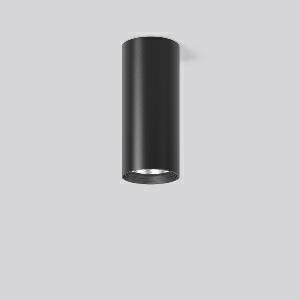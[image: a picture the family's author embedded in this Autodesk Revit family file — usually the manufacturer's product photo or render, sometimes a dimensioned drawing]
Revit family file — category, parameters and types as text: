
# Revit family: heledon_mini_a_931201_003_3_76_2d51
name_source: partatom
category: Lighting Fixtures
units: mm (PartAtom-declared; Revit-internal decimal feet)

## family parameters
Cut with Voids When Loaded = No
Host = Face
Light Source = No
Part Type = Normal
Room Calculation Point = No
Round Connector Dimension = Use Diameter
Shared = No

## types (1)
- HELEDON mini A (1 x LED Modul 935, 2500 lm, 3500)
    Apparent Load = 20 VA
    Approval mark = CE
    CIE Flux Codes = 99 100 100 100 100
    Color Rendering = 92
    Color Temperature = 3500
    Default Elevation = 1800 mm
    Description = Series: HELEDON mini
Cylindrical surface-mounted downlight. Housing: die-cast aluminium, powder-coated. Internal ceiling frame polycarbonate with bayonet mounting. Black plastic ring and recessed LED to prevent glare from the side. Optical assembly with reflector made of MIRO-Silver with 98% total light reflection for outstanding efficiency - can be changed without tools. Best colour rendering index Ra>90. Suitable for Ceiling mounting. Easy installation with a separate ceiling frame with bayonet mounting and plug connection. Driver integrated. Connected via plug-in connector. High quality converter without flickering and stroboscopic effect. The following accessories can be mounted without use of tools: interchangeable lenses, decorative glasses, honeycomb louvre, clear and frosted diffusers, white interchangeable plastic ring. 
Colour: deep black, matt (RAL 9005)
Diameter: 87 mm
Height: 197 mm
Lamp: LED
Socket: without socket
Colour temperature: 3500K
Colour rendering index (CRI): 92
System power: 20 W
Rated luminous flux: 2500 lm
Luminous efficiency: 125 lm/W
Control gear: Converter, dimmable, DALI
Protection class: I
Type of protection: IP 20
    Height = 197 mm
    Lamp = 1 x LED Modul 935
    Lamp Light Flux = 2500 lm
    Lamp count = 1
    Length = 87 mm
    Lifetime = 50000 h
    Luminous efficacy = 125 lm/W
    Manufacturer = RZB
    ModVariant = No
    Model = 931201.003.3.76
    Mounting Place = Ceiling
    Mounting Type = Surface mounted
    Number of Poles = 1
    OnlyDefault = Yes
    Power Factor = 1
    Product Name = HELEDON mini A
    Product group = Surface mounted downlights
    ProductGroupID = 302
    Protection Class = Protection class I
    Protection Degree = IP 20
    RLX_Detail_Level = 1
    RLX_Emergency_Light_Flux = 0 lm
    RLX_Emergency_Type = 0
    RLX_Emergency_Type_DB = No
    RlxData = <blob elided: 107421 chars, md5=161cb593>
    Socket = socket
    Standby Power = 0 W
    System Light Flux = 2500 lm
    System Power = 20 W
    Type Comments = Product without accessories
    Type Image = 931188.003.jpg
    URL = http://relux.com
    VarID = ---
    Voltage = 230 V
    Voltage Range = 220-240 V
    Weight = 0.00 kg
    Width = 0 mm  [stored 0 ft]

note: [stored X ft] marks values corroborated as IEEE doubles in the binary element streams (Revit-internal decimal feet)

## geometry (parser evidence)
native form markers: Blend x4, Sweep x11
no freeform markers — native parametric forms only
